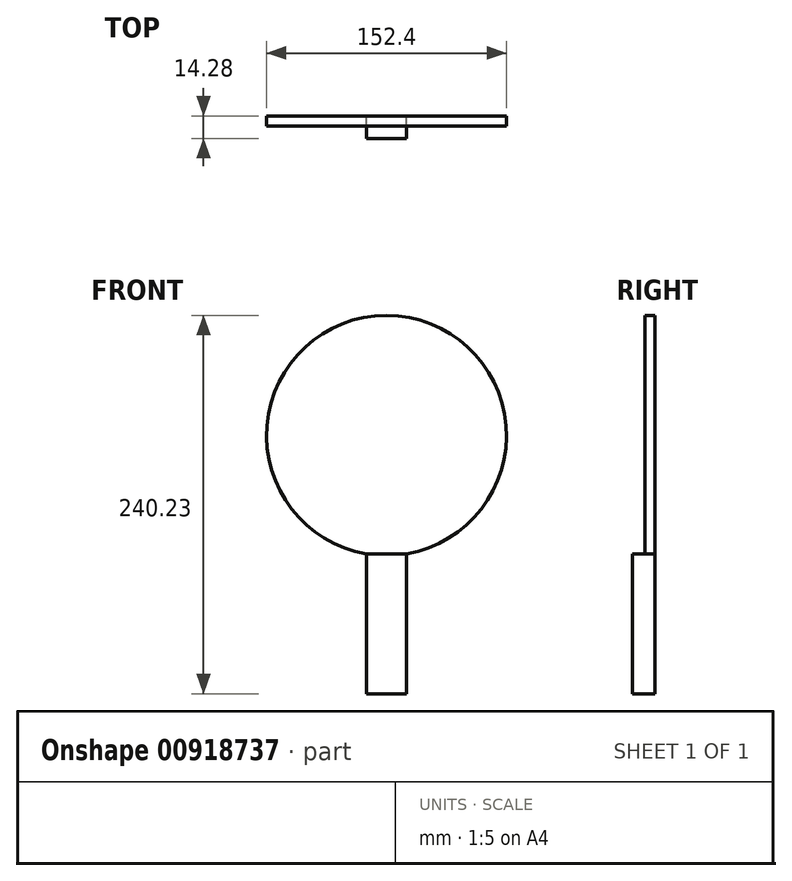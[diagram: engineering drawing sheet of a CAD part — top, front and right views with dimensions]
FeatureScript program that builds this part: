
annotation { "Feature Type Name" : "Feature", "Feature Type Description" : "" }
export const myFeature = defineFeature(function(context is Context, id is Id, definition is map)
    precondition{}
    {
        {
            var Q0;
            Q0=qCreatedBy(makeId("Front.planeOp"),FACE);
            var sketch = newSketch(context, id + "F0", { "sketchPlane" : qUnion([Q0])});
            skLineSegment(sketch, "E0.bottom", {"start": v(-12.7, 0) * mm, "end": v(12.7, 0) * mm});
            skLineSegment(sketch, "E0.left", {"start": v(-12.7, 0) * mm, "end": v(-12.7, 88.9) * mm});
            skLineSegment(sketch, "E0.right", {"start": v(12.7, 0) * mm, "end": v(12.7, 88.9) * mm});
            skPoint(sketch, "E1", {"position": v(0, 164.03) * mm});
            skLineSegment(sketch, "E2", {"start": v(-12.7, 88.9) * mm, "end": v(12.7, 88.9) * mm, "construction": true});
            skArc(sketch, "E3", {"start": v(12.7, 88.9) * mm, "mid": v(0, 240.23) * mm, "end": v(-12.7, 88.9) * mm});
            skSolve(sketch);
        }
        {
            var Q0;
            Q0 = qSketchRegion(id + "F0", true);
            extrude(context, id + "F1", {"entities" : qUnion([Q0]), "endBound" : BoundingType.SYMMETRIC, "depth" : 6.35 * mm, "offsetDistance" : 25.4 * mm});
        }
        {
            var Q0;
            Q0=makeQuery(id+"F1.opExtrude","CAP_FACE",FACE,{"disambiguationData":[OSD([sQuery(id+"F0.wireOp",EDGE,"E0.bottom"),sQuery(id+"F0.wireOp",EDGE,"E0.left"),sQuery(id+"F0.wireOp",EDGE,"E0.right"),sQuery(id+"F0.wireOp",EDGE,"E3")])],"isStart":false});
            var sketch = newSketch(context, id + "F2", { "sketchPlane" : qUnion([Q0])});
            skLineSegment(sketch, "E4", {"start": v(-12.7, 0) * mm, "end": v(-12.7, 88.9) * mm});
            skLineSegment(sketch, "E5", {"start": v(-12.7, 88.9) * mm, "end": v(12.7, 88.9) * mm});
            skLineSegment(sketch, "E6", {"start": v(12.7, 88.9) * mm, "end": v(12.7, 0) * mm});
            skLineSegment(sketch, "E7", {"start": v(12.7, 0) * mm, "end": v(-12.7, 0) * mm});
            skSolve(sketch);
        }
        {
            var Q0;
            Q0 = qSketchRegion(id + "F2", true);
            extrude(context, id + "F3", {"entities" : qUnion([Q0]), "operationType" : NewBodyOperationType.ADD, "depth" : 7.94 * mm, "offsetDistance" : 25.4 * mm});
        }
    });
